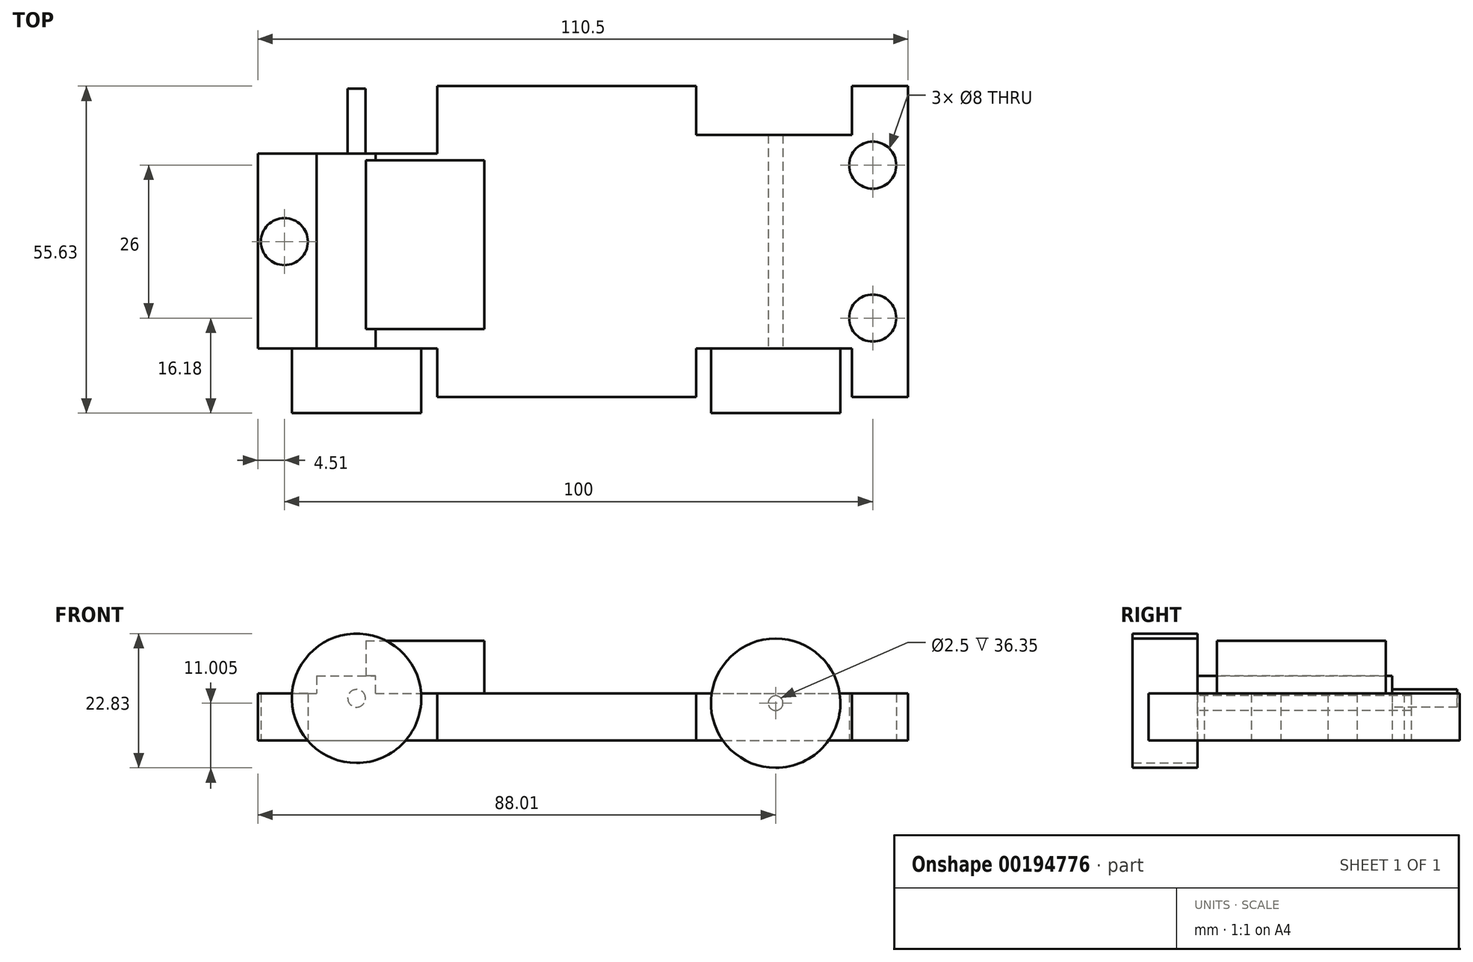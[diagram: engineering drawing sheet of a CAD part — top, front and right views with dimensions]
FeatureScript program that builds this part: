
annotation { "Feature Type Name" : "Feature", "Feature Type Description" : "" }
export const myFeature = defineFeature(function(context is Context, id is Id, definition is map)
    precondition{}
    {
        {
            var Q0;
            Q0=qCreatedBy(makeId("Top.planeOp"),FACE);
            var sketch = newSketch(context, id + "F0", { "sketchPlane" : qUnion([Q0])});
            skLineSegment(sketch, "E0.bottom", {"start": v(55.25, 26.46) * mm, "end": v(45.74, 26.46) * mm});
            skLineSegment(sketch, "E0.top", {"start": v(55.25, -26.46) * mm, "end": v(45.74, -26.46) * mm});
            skLineSegment(sketch, "E0.left", {"start": v(55.25, 26.46) * mm, "end": v(55.25, -26.46) * mm});
            skLineSegment(sketch, "E0.right", {"start": v(-55.25, 14.95) * mm, "end": v(-55.25, -18.18) * mm});
            skPoint(sketch, "E0.middle", {"position": v(0, 0) * mm});
            skCircle(sketch, "E1", {"center": v(-50.74, 0) * mm, "radius": 4 * mm});
            skCircle(sketch, "E2", {"center": v(49.26, 13) * mm, "radius": 4 * mm});
            skCircle(sketch, "E3.MirrorC", {"center": v(49.26, -13) * mm, "radius": 4 * mm});
            skLineSegment(sketch, "E4.top", {"start": v(-55.25, 14.95) * mm, "end": v(-24.73, 14.96) * mm});
            skLineSegment(sketch, "E4.right", {"start": v(-24.73, 26.45) * mm, "end": v(-24.73, 14.96) * mm});
            skLineSegment(sketch, "E5.top", {"start": v(-55.25, -18.18) * mm, "end": v(-24.75, -18.18) * mm});
            skLineSegment(sketch, "E5.right", {"start": v(-24.75, -26.46) * mm, "end": v(-24.75, -18.18) * mm});
            skLineSegment(sketch, "E6.top", {"start": v(19.25, 18.18) * mm, "end": v(45.74, 18.18) * mm});
            skLineSegment(sketch, "E6.left", {"start": v(19.25, 26.46) * mm, "end": v(19.25, 18.18) * mm});
            skLineSegment(sketch, "E6.right", {"start": v(45.74, 26.46) * mm, "end": v(45.74, 18.18) * mm});
            skLineSegment(sketch, "E7.MirrorCS", {"start": v(19.25, -18.18) * mm, "end": v(45.74, -18.18) * mm});
            skLineSegment(sketch, "E8.MirrorCS", {"start": v(19.25, -26.46) * mm, "end": v(19.25, -18.18) * mm});
            skLineSegment(sketch, "E9.MirrorCS", {"start": v(45.74, -26.46) * mm, "end": v(45.74, -18.18) * mm});
            skPoint(sketch, "E10.orphan", {"position": v(-55.25, 26.46) * mm});
            skPoint(sketch, "E11.orphan", {"position": v(-55.25, -26.46) * mm});
            skLineSegment(sketch, "E12.trimOffspring", {"start": v(19.25, -26.46) * mm, "end": v(-24.75, -26.46) * mm});
            skLineSegment(sketch, "E13.trimOffspring", {"start": v(19.25, 26.46) * mm, "end": v(-24.73, 26.46) * mm});
            skSolve(sketch);
        }
        {
            var Q0;
            Q0 = qSketchRegion(id + "F0", true);
            extrude(context, id + "F1", {"entities" : qUnion([Q0]), "depth" : 8 * mm});
        }
        {
            var Q0;
            Q0=makeQuery(id+"F1.opExtrude","CAP_FACE",FACE,{"disambiguationData":[OSD([sQuery(id+"F0.wireOp",EDGE,"E0.bottom"),sQuery(id+"F0.wireOp",EDGE,"E0.top"),sQuery(id+"F0.wireOp",EDGE,"E0.left"),sQuery(id+"F0.wireOp",EDGE,"E0.right"),sQuery(id+"F0.wireOp",EDGE,"E1"),sQuery(id+"F0.wireOp",EDGE,"E2"),sQuery(id+"F0.wireOp",EDGE,"E3.MirrorC"),sQuery(id+"F0.wireOp",EDGE,"E4.top"),sQuery(id+"F0.wireOp",EDGE,"E4.right"),sQuery(id+"F0.wireOp",EDGE,"E5.top"),sQuery(id+"F0.wireOp",EDGE,"E5.right"),sQuery(id+"F0.wireOp",EDGE,"E6.top"),sQuery(id+"F0.wireOp",EDGE,"E6.left"),sQuery(id+"F0.wireOp",EDGE,"E6.right"),sQuery(id+"F0.wireOp",EDGE,"E7.MirrorCS"),sQuery(id+"F0.wireOp",EDGE,"E8.MirrorCS"),sQuery(id+"F0.wireOp",EDGE,"E9.MirrorCS"),sQuery(id+"F0.wireOp",EDGE,"E12.trimOffspring"),sQuery(id+"F0.wireOp",EDGE,"E13.trimOffspring")])],"isStart":false});
            var sketch = newSketch(context, id + "F2", { "sketchPlane" : qUnion([Q0])});
            skLineSegment(sketch, "E14.bottom", {"start": v(-45.25, 14.95) * mm, "end": v(-35.25, 14.96) * mm});
            skLineSegment(sketch, "E14.top", {"start": v(-45.25, -18.18) * mm, "end": v(-35.25, -18.18) * mm});
            skLineSegment(sketch, "E14.left", {"start": v(-45.25, 14.95) * mm, "end": v(-45.25, -18.18) * mm});
            skLineSegment(sketch, "E14.right", {"start": v(-35.25, 14.96) * mm, "end": v(-35.25, -18.18) * mm});
            skSolve(sketch);
        }
        {
            var Q0;
            Q0 = qSketchRegion(id + "F2", true);
            extrude(context, id + "F3", {"entities" : qUnion([Q0]), "operationType" : NewBodyOperationType.ADD, "depth" : 3 * mm});
        }
        {
            var Q0;
            Q0=qCreatedBy(makeId("Front.planeOp"),FACE);
            var sketch = newSketch(context, id + "F4", { "sketchPlane" : qUnion([Q0])});
            skCircle(sketch, "E15", {"center": v(-38.47, 7.2) * mm, "radius": 1.5 * mm});
            skSolve(sketch);
        }
        {
            var Q0;
            Q0 = qSketchRegion(id + "F4", true);
            extrude(context, id + "F5", {"entities" : qUnion([Q0]), "operationType" : NewBodyOperationType.ADD, "endBound" : BoundingType.SYMMETRIC, "oppositeDirection" : true, "depth" : 52 * mm});
        }
        {
            var Q0;
            {var subQ0=sQuery(id+"F0.wireOp",EDGE,"E6.top");var subQ1=sQuery(id+"F0.wireOp",EDGE,"E12.trimOffspring");var subQ2=sQuery(id+"F0.wireOp",EDGE,"E13.trimOffspring");var subQ3=sQuery(id+"F0.wireOp",EDGE,"E5.right");var subQ4=sQuery(id+"F0.wireOp",EDGE,"E5.top");var subQ5=sQuery(id+"F0.wireOp",EDGE,"E9.MirrorCS");var subQ6=sQuery(id+"F0.wireOp",EDGE,"E4.top");var subQ7=sQuery(id+"F0.wireOp",EDGE,"E7.MirrorCS");var subQ8=sQuery(id+"F0.wireOp",EDGE,"E3.MirrorC");var subQ9=sQuery(id+"F0.wireOp",EDGE,"E0.bottom");var subQ10=sQuery(id+"F0.wireOp",EDGE,"E4.right");var subQ11=sQuery(id+"F0.wireOp",EDGE,"E8.MirrorCS");var subQ12=sQuery(id+"F0.wireOp",EDGE,"E0.top");var subQ13=sQuery(id+"F0.wireOp",EDGE,"E0.left");var subQ14=sQuery(id+"F0.wireOp",EDGE,"E2");var subQ15=sQuery(id+"F0.wireOp",EDGE,"E6.left");var subQ16=sQuery(id+"F0.wireOp",EDGE,"E6.right");Q0=makeQuery(id+"F3.boolean.opBoolean","SPLIT",FACE,{"disambiguationData":[TD([makeQuery(id+"F1.opExtrude","SWEPT_FACE",FACE,{"disambiguationData":[OSD([subQ9])]})])],"derivedFrom":makeQuery(id+"F1.opExtrude","CAP_FACE",FACE,{"disambiguationData":[OSD([subQ9,subQ12,subQ13,sQuery(id+"F0.wireOp",EDGE,"E0.right"),sQuery(id+"F0.wireOp",EDGE,"E1"),subQ14,subQ8,subQ6,subQ10,subQ4,subQ3,subQ0,subQ15,subQ16,subQ7,subQ11,subQ5,subQ1,subQ2])],"isStart":false})});}
            var sketch = newSketch(context, id + "F6", { "sketchPlane" : qUnion([Q0])});
            skLineSegment(sketch, "E16.bottom", {"start": v(-36.9, 13.86) * mm, "end": v(-16.75, 13.86) * mm});
            skLineSegment(sketch, "E16.top", {"start": v(-36.9, -14.86) * mm, "end": v(-16.75, -14.86) * mm});
            skLineSegment(sketch, "E16.left", {"start": v(-36.9, 13.86) * mm, "end": v(-36.9, -14.86) * mm});
            skLineSegment(sketch, "E16.right", {"start": v(-16.75, 13.86) * mm, "end": v(-16.75, -14.86) * mm});
            skSolve(sketch);
        }
        {
            var Q0;
            Q0 = qSketchRegion(id + "F6", true);
            extrude(context, id + "F7", {"entities" : qUnion([Q0]), "operationType" : NewBodyOperationType.ADD, "depth" : 9 * mm});
        }
        {
            var Q0;
            Q0=makeQuery(id+"F3.boolean.opBoolean","MERGE",FACE,{"derivedFrom":[makeQuery(id+"F1.opExtrude","SWEPT_FACE",FACE,{"disambiguationData":[OSD([sQuery(id+"F0.wireOp",EDGE,"E5.top")])]}),makeQuery(id+"F3.opExtrude","SWEPT_FACE",FACE,{"disambiguationData":[OSD([sQuery(id+"F2.wireOp",EDGE,"E14.top")])]})]});
            var sketch = newSketch(context, id + "F8", { "sketchPlane" : qUnion([Q0])});
            skCircle(sketch, "E17", {"center": v(-38.47, 7.2) * mm, "radius": 11 * mm});
            skSolve(sketch);
        }
        {
            var Q0;
            Q0 = qSketchRegion(id + "F8", true);
            extrude(context, id + "F9", {"entities" : qUnion([Q0]), "operationType" : NewBodyOperationType.ADD, "depth" : 11 * mm});
        }
        {
            var Q0;
            Q0=makeQuery(id+"F1.opExtrude","SWEPT_FACE",FACE,{"disambiguationData":[OSD([sQuery(id+"F0.wireOp",EDGE,"E7.MirrorCS")])]});
            var sketch = newSketch(context, id + "F10", { "sketchPlane" : qUnion([Q0])});
            skCircle(sketch, "E18", {"center": v(32.76, 6.38) * mm, "radius": 1.25 * mm});
            skSolve(sketch);
        }
        {
            var Q0;
            Q0 = qSketchRegion(id + "F10", true);
            extrude(context, id + "F11", {"entities" : qUnion([Q0]), "operationType" : NewBodyOperationType.REMOVE, "endBound" : BoundingType.THROUGH_ALL, "oppositeDirection" : true, "depth" : 25 * mm});
        }
        {
            var Q0;
            Q0=makeQuery(id+"F1.opExtrude","SWEPT_FACE",FACE,{"disambiguationData":[OSD([sQuery(id+"F0.wireOp",EDGE,"E7.MirrorCS")])]});
            var sketch = newSketch(context, id + "F12", { "sketchPlane" : qUnion([Q0])});
            skCircle(sketch, "E19", {"center": v(32.76, 6.38) * mm, "radius": 11 * mm});
            skSolve(sketch);
        }
        {
            var Q0;
            Q0 = qSketchRegion(id + "F12", true);
            extrude(context, id + "F13", {"entities" : qUnion([Q0]), "operationType" : NewBodyOperationType.ADD, "depth" : 11 * mm});
        }
    });
